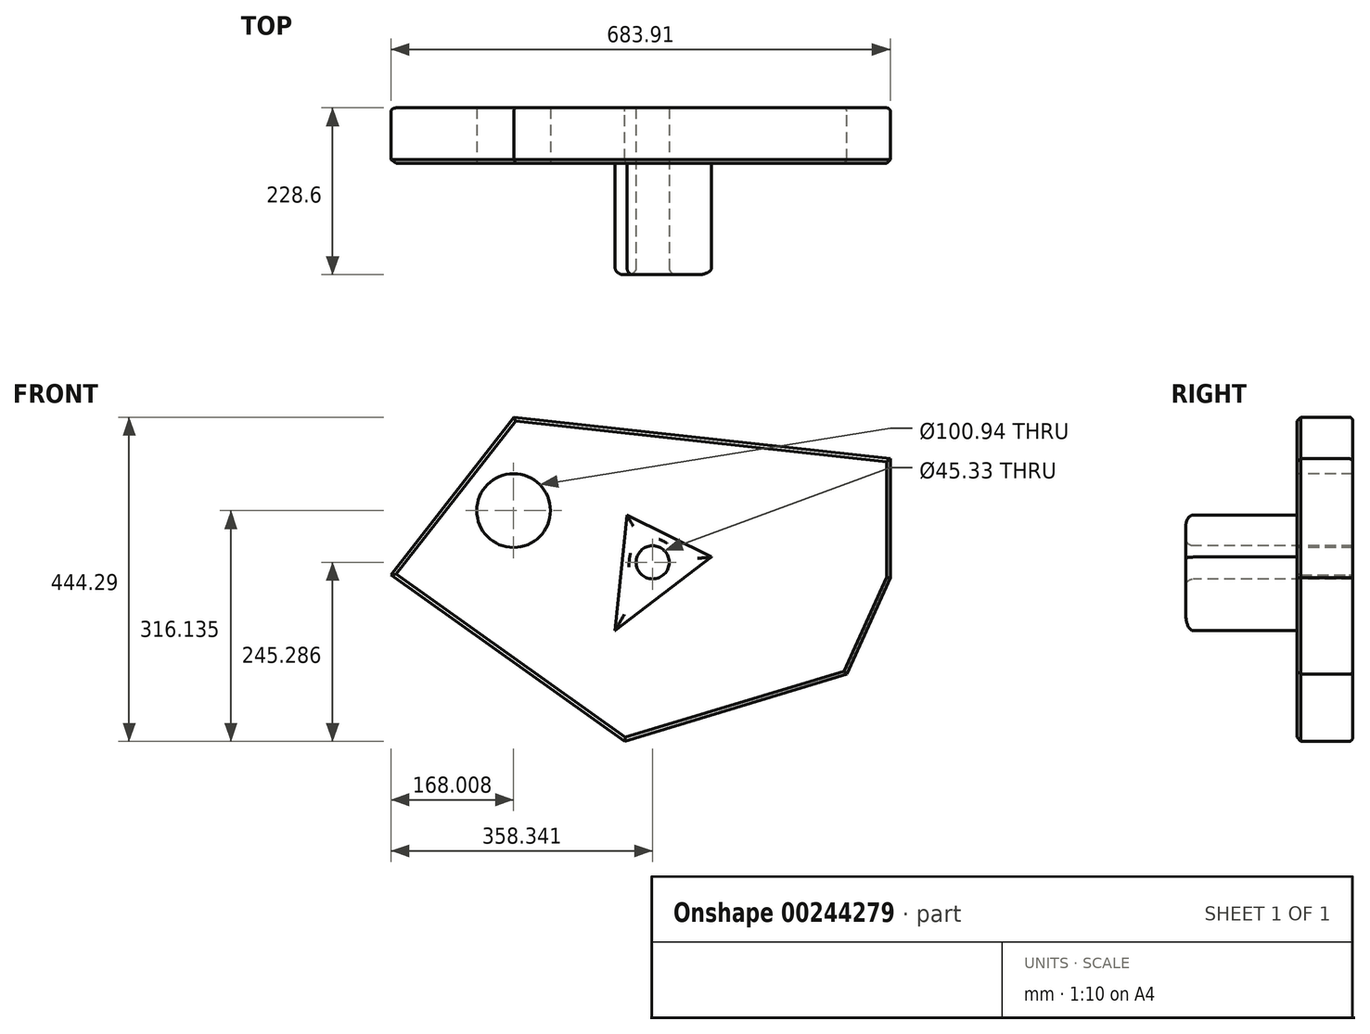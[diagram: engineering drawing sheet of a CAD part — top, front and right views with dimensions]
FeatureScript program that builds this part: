
annotation { "Feature Type Name" : "Feature", "Feature Type Description" : "" }
export const myFeature = defineFeature(function(context is Context, id is Id, definition is map)
    precondition{}
    {
        {
            var Q0;
            Q0=qCreatedBy(makeId("Front.planeOp"),FACE);
            var sketch = newSketch(context, id + "F0", { "sketchPlane" : qUnion([Q0])});
            skLineSegment(sketch, "E0", {"start": v(-138.55, 237) * mm, "end": v(376.98, 180.02) * mm});
            skLineSegment(sketch, "E1", {"start": v(376.98, 180.02) * mm, "end": v(376.98, 16.8) * mm});
            skLineSegment(sketch, "E2", {"start": v(376.98, 16.8) * mm, "end": v(317.4, -115.31) * mm});
            skLineSegment(sketch, "E3", {"start": v(317.4, -115.31) * mm, "end": v(13, -207.28) * mm});
            skLineSegment(sketch, "E4", {"start": v(13, -207.28) * mm, "end": v(-306.93, 20.7) * mm});
            skLineSegment(sketch, "E5", {"start": v(-306.93, 20.7) * mm, "end": v(-138.55, 237) * mm});
            skSolve(sketch);
        }
        {
            var Q0;
            Q0=makeQuery(id+"F0.imprint","IMPRINT",FACE,{"disambiguationData":[TD([[makeQuery(id+"F0.imprint","IMPRINT",EDGE,{"derivedFrom":sQuery(id+"F0.wireOp",EDGE,"E0")}),-1.0]])]});
            extrude(context, id + "F1", {"entities" : qUnion([Q0]), "depth" : 76.2 * mm});
        }
        {
            var Q0;
            Q0=makeQuery(id+"F1.opExtrude","CAP_EDGE",EDGE,{"disambiguationData":[OSD([sQuery(id+"F0.wireOp",EDGE,"E4")])],"isStart":false});
            var Q1;
            Q1=makeQuery(id+"F1.opExtrude","CAP_EDGE",EDGE,{"disambiguationData":[OSD([sQuery(id+"F0.wireOp",EDGE,"E3")])],"isStart":false});
            var Q2;
            Q2=makeQuery(id+"F1.opExtrude","CAP_EDGE",EDGE,{"disambiguationData":[OSD([sQuery(id+"F0.wireOp",EDGE,"E2")])],"isStart":false});
            var Q3;
            Q3=makeQuery(id+"F1.opExtrude","CAP_EDGE",EDGE,{"disambiguationData":[OSD([sQuery(id+"F0.wireOp",EDGE,"E1")])],"isStart":false});
            var Q4;
            Q4=makeQuery(id+"F1.opExtrude","CAP_EDGE",EDGE,{"disambiguationData":[OSD([sQuery(id+"F0.wireOp",EDGE,"E0")])],"isStart":false});
            var Q5;
            Q5=makeQuery(id+"F1.opExtrude","CAP_EDGE",EDGE,{"disambiguationData":[OSD([sQuery(id+"F0.wireOp",EDGE,"E5")])],"isStart":false});
            chamfer(context, id + "F2", {"entities" : qUnion([Q0, Q1, Q2, Q3, Q4, Q5]), "width" : 5.08 * mm, "tangentPropagation" : true});
        }
        {
            var Q0;
            Q0=makeQuery(id+"F1.opExtrude","CAP_FACE",FACE,{"disambiguationData":[OSD([sQuery(id+"F0.wireOp",EDGE,"E0"),sQuery(id+"F0.wireOp",EDGE,"E1"),sQuery(id+"F0.wireOp",EDGE,"E2"),sQuery(id+"F0.wireOp",EDGE,"E3"),sQuery(id+"F0.wireOp",EDGE,"E4"),sQuery(id+"F0.wireOp",EDGE,"E5")])],"isStart":false});
            var sketch = newSketch(context, id + "F3", { "sketchPlane" : qUnion([Q0])});
            skLineSegment(sketch, "E6", {"start": v(16.3, 102.79) * mm, "end": v(132.25, 45.25) * mm});
            skLineSegment(sketch, "E7", {"start": v(132.25, 45.25) * mm, "end": v(0, -55.66) * mm});
            skLineSegment(sketch, "E8", {"start": v(0, -55.66) * mm, "end": v(16.3, 102.79) * mm});
            skSolve(sketch);
        }
        {
            var Q0;
            Q0=makeQuery(id+"F3.imprint","IMPRINT",FACE,{"disambiguationData":[TD([[makeQuery(id+"F3.imprint","IMPRINT",EDGE,{"derivedFrom":sQuery(id+"F3.wireOp",EDGE,"E6")}),-1.0]])]});
            extrude(context, id + "F4", {"entities" : qUnion([Q0]), "operationType" : NewBodyOperationType.ADD, "depth" : 152.4 * mm});
        }
        {
            var Q0;
            Q0=makeQuery(id+"F1.opExtrude","CAP_FACE",FACE,{"disambiguationData":[OSD([sQuery(id+"F0.wireOp",EDGE,"E0"),sQuery(id+"F0.wireOp",EDGE,"E1"),sQuery(id+"F0.wireOp",EDGE,"E2"),sQuery(id+"F0.wireOp",EDGE,"E3"),sQuery(id+"F0.wireOp",EDGE,"E4"),sQuery(id+"F0.wireOp",EDGE,"E5")])],"isStart":false});
            var sketch = newSketch(context, id + "F5", { "sketchPlane" : qUnion([Q0])});
            skCircle(sketch, "E9", {"center": v(-138.92, 108.85) * mm, "radius": 50.47 * mm});
            skSolve(sketch);
        }
        {
            var Q0;
            Q0=makeQuery(id+"F5.imprint","IMPRINT",FACE,{"disambiguationData":[TD([[makeQuery(id+"F5.imprint","IMPRINT",EDGE,{"derivedFrom":sQuery(id+"F5.wireOp",EDGE,"E9")}),1.0]])]});
            extrude(context, id + "F6", {"entities" : qUnion([Q0]), "operationType" : NewBodyOperationType.REMOVE, "oppositeDirection" : true, "depth" : 76.2 * mm});
        }
        {
            var Q0;
            Q0=makeQuery(id+"F4.opExtrude","CAP_FACE",FACE,{"disambiguationData":[OSD([sQuery(id+"F3.wireOp",EDGE,"E6"),sQuery(id+"F3.wireOp",EDGE,"E7"),sQuery(id+"F3.wireOp",EDGE,"E8")])],"isStart":false});
            var sketch = newSketch(context, id + "F7", { "sketchPlane" : qUnion([Q0])});
            skCircle(sketch, "E10", {"center": v(51.41, 38) * mm, "radius": 22.66 * mm});
            skSolve(sketch);
        }
        {
            var Q0;
            Q0=makeQuery(id+"F7.imprint","IMPRINT",FACE,{"disambiguationData":[TD([[makeQuery(id+"F7.imprint","IMPRINT",EDGE,{"derivedFrom":sQuery(id+"F7.wireOp",EDGE,"E10")}),1.0]])]});
            extrude(context, id + "F8", {"entities" : qUnion([Q0]), "operationType" : NewBodyOperationType.REMOVE, "oppositeDirection" : true, "depth" : 228.6 * mm});
        }
        {
            var Q0;
            Q0=makeQuery(id+"F1.opExtrude","CAP_EDGE",EDGE,{"disambiguationData":[OSD([sQuery(id+"F0.wireOp",EDGE,"E4")])],"isStart":true});
            var Q1;
            Q1=makeQuery(id+"F1.opExtrude","CAP_EDGE",EDGE,{"disambiguationData":[OSD([sQuery(id+"F0.wireOp",EDGE,"E3")])],"isStart":true});
            var Q2;
            Q2=makeQuery(id+"F1.opExtrude","CAP_EDGE",EDGE,{"disambiguationData":[OSD([sQuery(id+"F0.wireOp",EDGE,"E2")])],"isStart":true});
            var Q3;
            Q3=makeQuery(id+"F1.opExtrude","CAP_EDGE",EDGE,{"disambiguationData":[OSD([sQuery(id+"F0.wireOp",EDGE,"E1")])],"isStart":true});
            var Q4;
            Q4=makeQuery(id+"F1.opExtrude","CAP_EDGE",EDGE,{"disambiguationData":[OSD([sQuery(id+"F0.wireOp",EDGE,"E0")])],"isStart":true});
            var Q5;
            Q5=makeQuery(id+"F1.opExtrude","CAP_EDGE",EDGE,{"disambiguationData":[OSD([sQuery(id+"F0.wireOp",EDGE,"E5")])],"isStart":true});
            fillet(context, id + "F9", {"entities" : qUnion([Q0, Q1, Q2, Q3, Q4, Q5]), "radius" : 5.08 * mm, "tangentPropagation" : true, "allowEdgeOverflow" : false});
        }
        {
            var Q0;
            Q0=makeQuery(id+"F4.opExtrude","CAP_FACE",FACE,{"disambiguationData":[OSD([sQuery(id+"F3.wireOp",EDGE,"E6"),sQuery(id+"F3.wireOp",EDGE,"E7"),sQuery(id+"F3.wireOp",EDGE,"E8")])],"isStart":false});
            fillet(context, id + "F10", {"entities" : qUnion([Q0]), "radius" : 10.16 * mm, "tangentPropagation" : true, "allowEdgeOverflow" : false});
        }
    });
